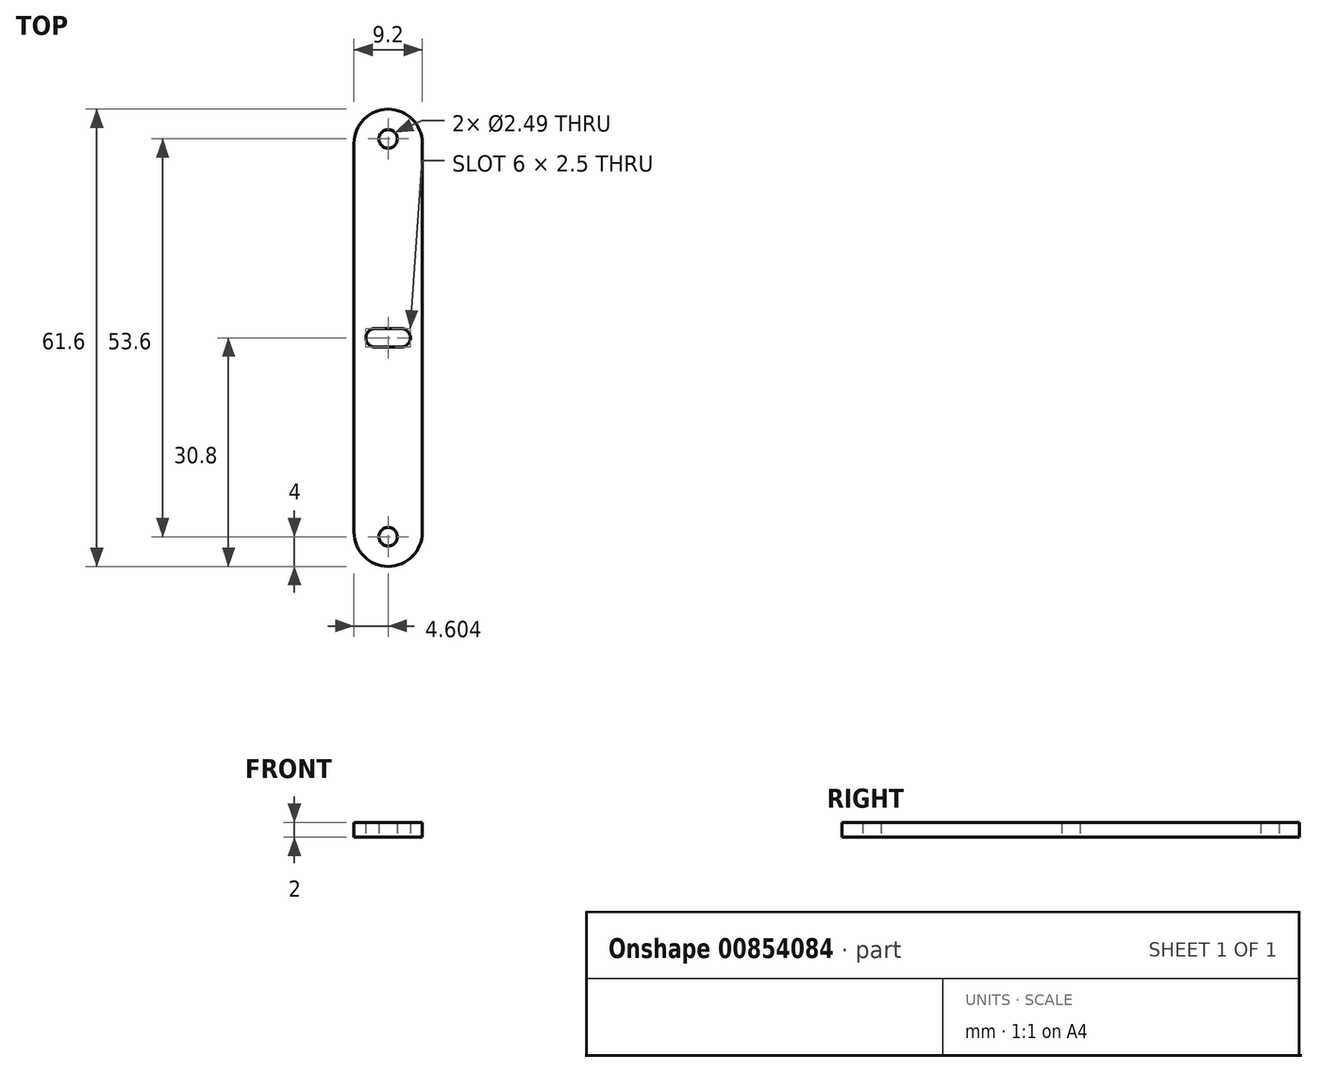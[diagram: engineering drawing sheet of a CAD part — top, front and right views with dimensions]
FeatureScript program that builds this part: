
annotation { "Feature Type Name" : "Feature", "Feature Type Description" : "" }
export const myFeature = defineFeature(function(context is Context, id is Id, definition is map)
    precondition{}
    {
        {
            var Q0;
            Q0=qCreatedBy(makeId("Top.planeOp"),FACE);
            var sketch = newSketch(context, id + "F0", { "sketchPlane" : qUnion([Q0])});
            skLineSegment(sketch, "E0", {"start": v(0, 0) * mm, "end": v(18.75, 0) * mm});
            skLineSegment(sketch, "E1", {"start": v(6.9, -47.95) * mm, "end": v(6.9, 41.47) * mm});
            skLineSegment(sketch, "E2", {"start": v(2.3, 0) * mm, "end": v(2.3, 26.2) * mm});
            skLineSegment(sketch, "E3.MirrorCS", {"start": v(11.5, 0) * mm, "end": v(11.5, 26.2) * mm});
            skLineSegment(sketch, "E4.MirrorCS", {"start": v(2.3, 0) * mm, "end": v(2.3, -26.2) * mm});
            skLineSegment(sketch, "E5.MirrorCS", {"start": v(11.5, 0) * mm, "end": v(11.5, -26.2) * mm});
            skArc(sketch, "E6", {"start": v(11.5, 26.2) * mm, "mid": v(6.9, 30.8) * mm, "end": v(2.3, 26.2) * mm});
            skArc(sketch, "E7.MirrorCS", {"start": v(11.5, -26.2) * mm, "mid": v(6.9, -30.8) * mm, "end": v(2.3, -26.2) * mm});
            skCircle(sketch, "E8", {"center": v(6.9, -26.8) * mm, "radius": 1.25 * mm});
            skCircle(sketch, "E9.MirrorC", {"center": v(6.9, 26.8) * mm, "radius": 1.25 * mm});
            skLineSegment(sketch, "E10", {"start": v(5.15, 1.25) * mm, "end": v(6.9, 1.25) * mm});
            skLineSegment(sketch, "E11.MirrorCS", {"start": v(5.15, -1.25) * mm, "end": v(6.9, -1.25) * mm});
            skArc(sketch, "E12", {"start": v(5.15, 1.25) * mm, "mid": v(3.9, 0) * mm, "end": v(5.15, -1.25) * mm});
            skLineSegment(sketch, "E13.MirrorCS", {"start": v(8.65, 1.25) * mm, "end": v(6.9, 1.25) * mm});
            skLineSegment(sketch, "E14.MirrorCS", {"start": v(8.65, -1.25) * mm, "end": v(6.9, -1.25) * mm});
            skArc(sketch, "E15.MirrorCS", {"start": v(8.65, 1.25) * mm, "mid": v(9.9, 0) * mm, "end": v(8.65, -1.25) * mm});
            skSolve(sketch);
        }
        {
            var Q0;
            Q0=qSketchRegion(id+"F0",true);
            extrude(context, id + "F1", {"entities" : qUnion([Q0]), "depth" : 2 * mm, "offsetDistance" : 25 * mm});
        }
    });
